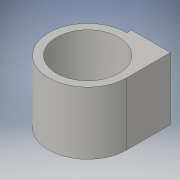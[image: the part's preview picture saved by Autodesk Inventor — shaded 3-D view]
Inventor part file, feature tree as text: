
AUTODESK INVENTOR PART (.ipt)
format: ipt  version: 2016 (Build 200138000, 138)  size: 117,248 bytes
history: native  units: in
note: dims shown in document units (in); Inventor stores cm internally (conversion verified against a paired STEP export)
features: extrude x3, sketch x3
ambient origin geometry x8: Origin, YZ Plane, XZ Plane, XY Plane, X Axis, Y Axis, Z Axis, Center Point
bodies: Solid1 (feature_tree)
feature tree (6):
  extrude  "Extrusion1"  Depth=1.25in
  extrude  "Extrusion2"  Depth=0.2in TaperAngle=0.0deg
  extrude  "Extrusion3"  Depth=0.2in
  sketch  "Sketch1"  dims[d0=1.0in d1=1.25in]
  sketch  "Sketch2"  dims[d2=0.2in d3=1.0in d4=0.0in]
  sketch  "Sketch3"  dims[d5=0.2in d6=0.3125in d7=0.515in d8=0.0in d9=0.25in d10=0.3125in d11=0.2in d12=0.0in]
